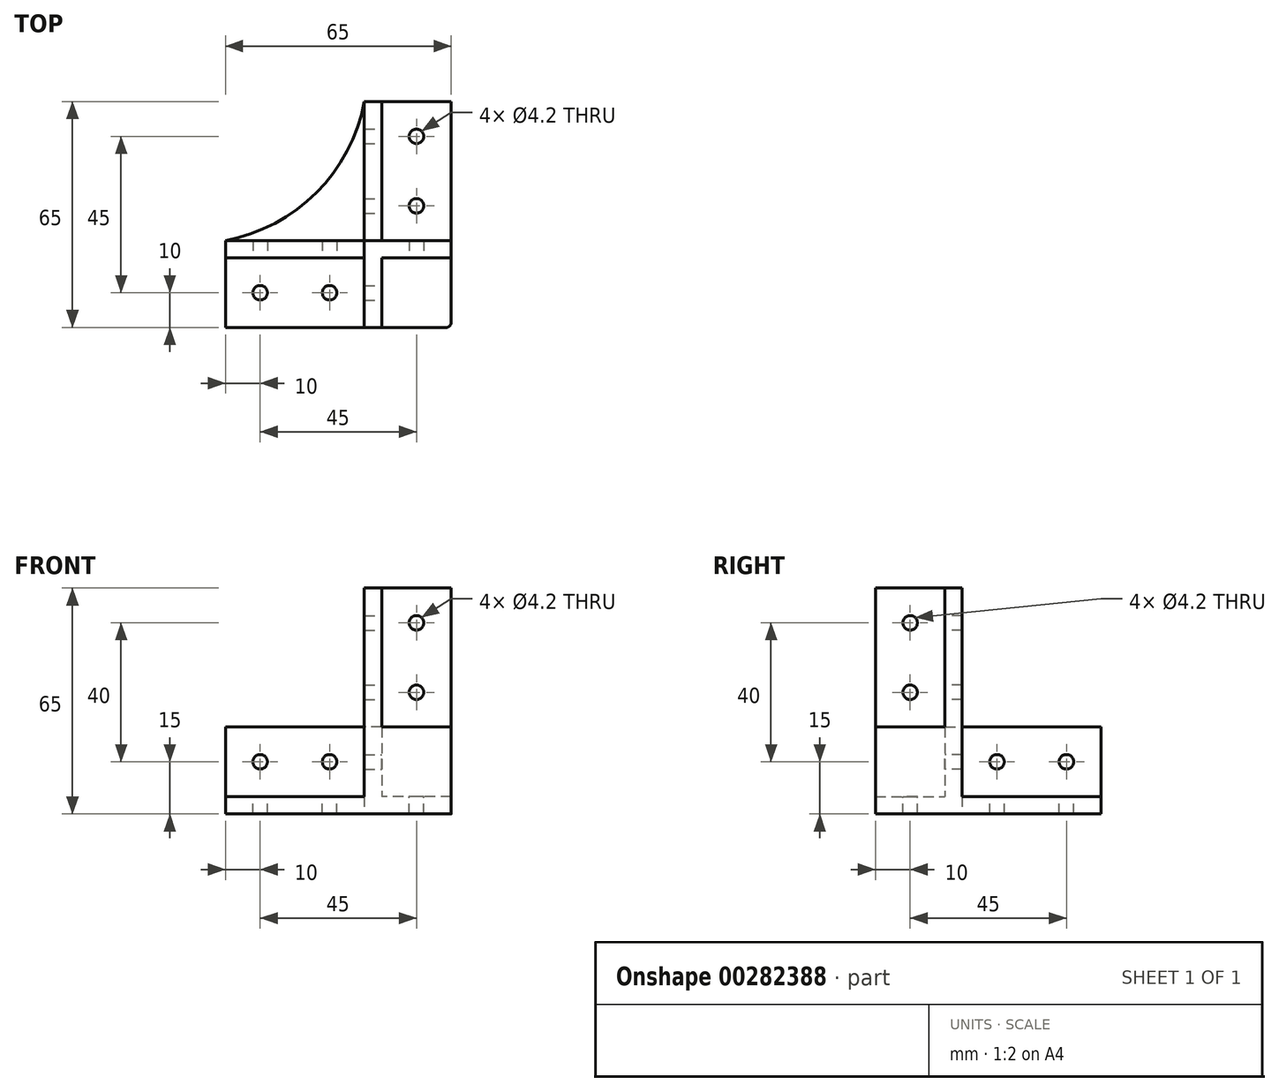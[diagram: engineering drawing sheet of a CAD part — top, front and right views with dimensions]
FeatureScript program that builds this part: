
annotation { "Feature Type Name" : "Feature", "Feature Type Description" : "" }
export const myFeature = defineFeature(function(context is Context, id is Id, definition is map)
    precondition{}
    {
        {
            var Q0;
            Q0=qCreatedBy(makeId("Top.planeOp"),FACE);
            var sketch = newSketch(context, id + "F0", { "sketchPlane" : qUnion([Q0])});
            skLineSegment(sketch, "E0", {"start": v(0, 0) * mm, "end": v(0, 65) * mm});
            skLineSegment(sketch, "E1", {"start": v(0, 65) * mm, "end": v(-25, 65) * mm});
            skLineSegment(sketch, "E2", {"start": v(0, 0) * mm, "end": v(-65, 0) * mm});
            skLineSegment(sketch, "E3", {"start": v(-65, 0) * mm, "end": v(-65, 25) * mm});
            skArc(sketch, "E4", {"start": v(-65, 25) * mm, "mid": v(-38.8, 38.8) * mm, "end": v(-25, 65) * mm});
            skSolve(sketch);
        }
        {
            var Q0;
            Q0=qSketchRegion(id+"F0",true);
            extrude(context, id + "F1", {"entities" : qUnion([Q0]), "depth" : 5 * mm});
        }
        {
            var Q0;
            Q0=makeQuery(id+"F1.opExtrude","CAP_FACE",FACE,{"disambiguationData":[OSD([sQuery(id+"F0.wireOp",EDGE,"E0"),sQuery(id+"F0.wireOp",EDGE,"E1"),sQuery(id+"F0.wireOp",EDGE,"E2"),sQuery(id+"F0.wireOp",EDGE,"E3"),sQuery(id+"F0.wireOp",EDGE,"E4")])],"isStart":false});
            var sketch = newSketch(context, id + "F2", { "sketchPlane" : qUnion([Q0])});
            skLineSegment(sketch, "E5", {"start": v(-65, 25) * mm, "end": v(-25, 25) * mm});
            skLineSegment(sketch, "E6", {"start": v(-25, 25) * mm, "end": v(-25, 65) * mm});
            skLineSegment(sketch, "E7", {"start": v(-25, 65) * mm, "end": v(-20, 65) * mm});
            skLineSegment(sketch, "E8", {"start": v(-20, 65) * mm, "end": v(-20, 25) * mm});
            skLineSegment(sketch, "E9", {"start": v(-20, 25) * mm, "end": v(0, 25) * mm});
            skLineSegment(sketch, "E10", {"start": v(0, 25) * mm, "end": v(0, 20) * mm});
            skLineSegment(sketch, "E11", {"start": v(0, 20) * mm, "end": v(-20, 20) * mm});
            skLineSegment(sketch, "E12", {"start": v(-20, 20) * mm, "end": v(-20, 0) * mm});
            skLineSegment(sketch, "E13", {"start": v(-20, 0) * mm, "end": v(-25, 0) * mm});
            skLineSegment(sketch, "E14", {"start": v(-25, 0) * mm, "end": v(-25, 20) * mm});
            skLineSegment(sketch, "E15", {"start": v(-25, 20) * mm, "end": v(-65, 20) * mm});
            skLineSegment(sketch, "E16", {"start": v(-65, 20) * mm, "end": v(-65, 25) * mm});
            skSolve(sketch);
        }
        {
            var Q0;
            Q0=qSketchRegion(id+"F2",true);
            extrude(context, id + "F3", {"entities" : qUnion([Q0]), "operationType" : NewBodyOperationType.ADD, "depth" : 20 * mm});
        }
        {
            var Q0;
            Q0=makeQuery(id+"F3.opExtrude","CAP_FACE",FACE,{"disambiguationData":[OSD([sQuery(id+"F2.wireOp",EDGE,"E5"),sQuery(id+"F2.wireOp",EDGE,"E6"),sQuery(id+"F2.wireOp",EDGE,"E7"),sQuery(id+"F2.wireOp",EDGE,"E8"),sQuery(id+"F2.wireOp",EDGE,"E9"),sQuery(id+"F2.wireOp",EDGE,"E10"),sQuery(id+"F2.wireOp",EDGE,"E11"),sQuery(id+"F2.wireOp",EDGE,"E12"),sQuery(id+"F2.wireOp",EDGE,"E13"),sQuery(id+"F2.wireOp",EDGE,"E14"),sQuery(id+"F2.wireOp",EDGE,"E15"),sQuery(id+"F2.wireOp",EDGE,"E16")])],"isStart":false});
            var sketch = newSketch(context, id + "F4", { "sketchPlane" : qUnion([Q0])});
            skLineSegment(sketch, "E17", {"start": v(-25, 25) * mm, "end": v(-25, 0) * mm});
            skLineSegment(sketch, "E18", {"start": v(-25, 0) * mm, "end": v(-20, 0) * mm});
            skLineSegment(sketch, "E19", {"start": v(-20, 0) * mm, "end": v(-20, 20) * mm});
            skLineSegment(sketch, "E20", {"start": v(-20, 20) * mm, "end": v(0, 20) * mm});
            skLineSegment(sketch, "E21", {"start": v(0, 20) * mm, "end": v(0, 25) * mm});
            skLineSegment(sketch, "E22", {"start": v(0, 25) * mm, "end": v(-25, 25) * mm});
            skSolve(sketch);
        }
        {
            var Q0;
            Q0=qSketchRegion(id+"F4",true);
            extrude(context, id + "F5", {"entities" : qUnion([Q0]), "operationType" : NewBodyOperationType.ADD, "depth" : 40 * mm});
        }
        {
            var Q0;
            {var subQ0=sQuery(id+"F0.wireOp",EDGE,"E2");var subQ1=sQuery(id+"F0.wireOp",EDGE,"E0");Q0=makeQuery(id+"F3.boolean.opBoolean","SPLIT",FACE,{"disambiguationData":[TD([makeQuery(id+"F3.opExtrude","SWEPT_FACE",FACE,{"disambiguationData":[OSD([sQuery(id+"F2.wireOp",EDGE,"E11")])]})])],"derivedFrom":makeQuery(id+"F1.opExtrude","CAP_FACE",FACE,{"disambiguationData":[OSD([subQ1,sQuery(id+"F0.wireOp",EDGE,"E1"),subQ0,sQuery(id+"F0.wireOp",EDGE,"E3"),sQuery(id+"F0.wireOp",EDGE,"E4")])],"isStart":false})});}
            var sketch = newSketch(context, id + "F6", { "sketchPlane" : qUnion([Q0])});
            skLineSegment(sketch, "E23.bottom", {"start": v(-20, 0) * mm, "end": v(0, 0) * mm});
            skLineSegment(sketch, "E23.top", {"start": v(-20, 20) * mm, "end": v(0, 20) * mm});
            skLineSegment(sketch, "E23.left", {"start": v(-20, 0) * mm, "end": v(-20, 20) * mm});
            skLineSegment(sketch, "E23.right", {"start": v(0, 0) * mm, "end": v(0, 20) * mm});
            skSolve(sketch);
        }
        {
            var Q0;
            Q0=qSketchRegion(id+"F6",true);
            extrude(context, id + "F7", {"entities" : qUnion([Q0]), "operationType" : NewBodyOperationType.ADD, "depth" : 20 * mm});
        }
        {
            var Q0;
            Q0=makeQuery(id+"F7.boolean.opBoolean","MERGE",EDGE,{"derivedFrom":[makeQuery(id+"F1.opExtrude","SWEPT_EDGE",EDGE,{"disambiguationData":[OSD([sQuery(id+"F0.wireOp",EDGE,"E0"),sQuery(id+"F0.wireOp",EDGE,"E2")])]}),makeQuery(id+"F7.opExtrude","SWEPT_EDGE",EDGE,{"disambiguationData":[OSD([sQuery(id+"F6.wireOp",EDGE,"E23.bottom"),sQuery(id+"F6.wireOp",EDGE,"E23.right")])]})]});
            fillet(context, id + "F8", {"entities" : qUnion([Q0]), "radius" : 1.5 * mm, "tangentPropagation" : true, "allowEdgeOverflow" : false});
        }
        {
            var Q0;
            Q0=makeQuery(id+"F3.opExtrude","SWEPT_FACE",FACE,{"disambiguationData":[OSD([sQuery(id+"F2.wireOp",EDGE,"E15")])]});
            var sketch = newSketch(context, id + "F9", { "sketchPlane" : qUnion([Q0])});
            skLineSegment(sketch, "E24", {"start": v(-65, 15) * mm, "end": v(-10, 15) * mm, "construction": true});
            skLineSegment(sketch, "E25", {"start": v(-10, 15) * mm, "end": v(-10, 65) * mm, "construction": true});
            skPoint(sketch, "E26", {"position": v(-55, 15) * mm});
            skPoint(sketch, "E27", {"position": v(-35, 15) * mm});
            skPoint(sketch, "E28", {"position": v(-10, 35) * mm});
            skPoint(sketch, "E29", {"position": v(-10, 55) * mm});
            skSolve(sketch);
        }
        {
            var Q0;
            Q0=makeQuery(id+"F5.boolean.opBoolean","MERGE",FACE,{"derivedFrom":[makeQuery(id+"F3.opExtrude","SWEPT_FACE",FACE,{"disambiguationData":[OSD([sQuery(id+"F2.wireOp",EDGE,"E12")])]}),makeQuery(id+"F5.opExtrude","SWEPT_FACE",FACE,{"disambiguationData":[OSD([sQuery(id+"F4.wireOp",EDGE,"E19")])]})]});
            var sketch = newSketch(context, id + "F10", { "sketchPlane" : qUnion([Q0])});
            skLineSegment(sketch, "E30", {"start": v(10, 65) * mm, "end": v(10, 15) * mm, "construction": true});
            skLineSegment(sketch, "E31", {"start": v(10, 15) * mm, "end": v(65, 15) * mm, "construction": true});
            skPoint(sketch, "E32", {"position": v(10, 55) * mm});
            skPoint(sketch, "E33", {"position": v(10, 35) * mm});
            skPoint(sketch, "E34", {"position": v(35, 15) * mm});
            skPoint(sketch, "E35", {"position": v(55, 15) * mm});
            skSolve(sketch);
        }
        {
            var Q0;
            {var subQ0=sQuery(id+"F0.wireOp",EDGE,"E3");var subQ1=sQuery(id+"F0.wireOp",EDGE,"E2");Q0=makeQuery(id+"F3.boolean.opBoolean","SPLIT",FACE,{"disambiguationData":[TD([makeQuery(id+"F3.opExtrude","SWEPT_FACE",FACE,{"disambiguationData":[OSD([sQuery(id+"F2.wireOp",EDGE,"E14")])]})])],"derivedFrom":makeQuery(id+"F1.opExtrude","CAP_FACE",FACE,{"disambiguationData":[OSD([sQuery(id+"F0.wireOp",EDGE,"E0"),sQuery(id+"F0.wireOp",EDGE,"E1"),subQ1,subQ0,sQuery(id+"F0.wireOp",EDGE,"E4")])],"isStart":false})});}
            var sketch = newSketch(context, id + "F11", { "sketchPlane" : qUnion([Q0])});
            skLineSegment(sketch, "E36", {"start": v(-65, 10) * mm, "end": v(-10, 10) * mm, "construction": true});
            skLineSegment(sketch, "E37", {"start": v(-10, 10) * mm, "end": v(-10, 65) * mm, "construction": true});
            skPoint(sketch, "E38", {"position": v(-55, 10) * mm});
            skPoint(sketch, "E39", {"position": v(-35, 10) * mm});
            skPoint(sketch, "E40", {"position": v(-10, 35) * mm});
            skPoint(sketch, "E41", {"position": v(-10, 55) * mm});
            skSolve(sketch);
        }
        {
            var Q0;
            Q0=sQuery(id+"F9.wireOp",VERTEX,"E26");
            var Q1;
            Q1=sQuery(id+"F9.wireOp",VERTEX,"E27");
            var Q2;
            Q2=sQuery(id+"F11.wireOp",VERTEX,"E39");
            var Q3;
            Q3=sQuery(id+"F11.wireOp",VERTEX,"E38");
            var Q4;
            Q4=sQuery(id+"F9.wireOp",VERTEX,"E28");
            var Q5;
            Q5=sQuery(id+"F9.wireOp",VERTEX,"E29");
            var Q6;
            Q6=sQuery(id+"F10.wireOp",VERTEX,"E33");
            var Q7;
            Q7=sQuery(id+"F10.wireOp",VERTEX,"E32");
            var Q8;
            Q8=sQuery(id+"F10.wireOp",VERTEX,"E34");
            var Q9;
            Q9=sQuery(id+"F10.wireOp",VERTEX,"E35");
            var Q10;
            Q10=sQuery(id+"F11.wireOp",VERTEX,"E41");
            var Q11;
            Q11=sQuery(id+"F11.wireOp",VERTEX,"E40");
            var Q12;
            Q12=makeQuery(id+"F1.opExtrude","SWEPT_BODY",BODY,{"disambiguationData":[OSD([sQuery(id+"F0.wireOp",EDGE,"E0"),sQuery(id+"F0.wireOp",EDGE,"E1"),sQuery(id+"F0.wireOp",EDGE,"E2"),sQuery(id+"F0.wireOp",EDGE,"E3"),sQuery(id+"F0.wireOp",EDGE,"E4")])]});
            hole(context, id + "F12", {"style" : HoleStyle.SIMPLE, "endStyle" : HoleEndStyle.THROUGH, "holeDiameter" : 4.2 * mm, "tappedDepth" : 3 * mm, "tapClearance" : 3, "startFromSketch" : true, "locations" : qUnion([Q0, Q1, Q2, Q3, Q4, Q5, Q6, Q7, Q8, Q9, Q10, Q11]), "scope" : qUnion([Q12])});
        }
        {
            var Q0;
            Q0=makeQuery(id+"F4Gvo9BevaE1wig_1.opFillet","SPLIT",FACE,{"disambiguationData":[OD(1.0)],"derivedFrom":makeQuery(id+"Fq6gnF7WoT1GwH2_1.opFillet","MERGE",FACE,{"derivedFrom":[makeQuery(id+"F3.opExtrude","SWEPT_FACE",FACE,{"disambiguationData":[OSD([sQuery(id+"F2.wireOp",EDGE,"E6")])]}),makeQuery(id+"F5.boolean.opBoolean","MERGE",FACE,{"derivedFrom":[makeQuery(id+"F3.opExtrude","SWEPT_FACE",FACE,{"disambiguationData":[OSD([sQuery(id+"F2.wireOp",EDGE,"E14")])]}),makeQuery(id+"F5.opExtrude","SWEPT_FACE",FACE,{"disambiguationData":[OSD([sQuery(id+"F4.wireOp",EDGE,"E17")])]})]})]})});
            var sketch = newSketch(context, id + "F13", { "sketchPlane" : qUnion([Q0])});
            skLineSegment(sketch, "E42", {"start": v(-10, 5) * mm, "end": v(-10, 15) * mm, "construction": true});
            skSolve(sketch);
        }
        {
            var Q0;
            Q0=makeQuery(id+"F5.boolean.opBoolean","MERGE",FACE,{"derivedFrom":[makeQuery(id+"F3.opExtrude","SWEPT_FACE",FACE,{"disambiguationData":[OSD([sQuery(id+"F2.wireOp",EDGE,"E9")])]}),makeQuery(id+"F5.opExtrude","SWEPT_FACE",FACE,{"disambiguationData":[OSD([sQuery(id+"F4.wireOp",EDGE,"E22")])]})]});
            var sketch = newSketch(context, id + "F14", { "sketchPlane" : qUnion([Q0])});
            skLineSegment(sketch, "E43", {"start": v(10, 5) * mm, "end": v(10, 15) * mm, "construction": true});
            skSolve(sketch);
        }
    });
